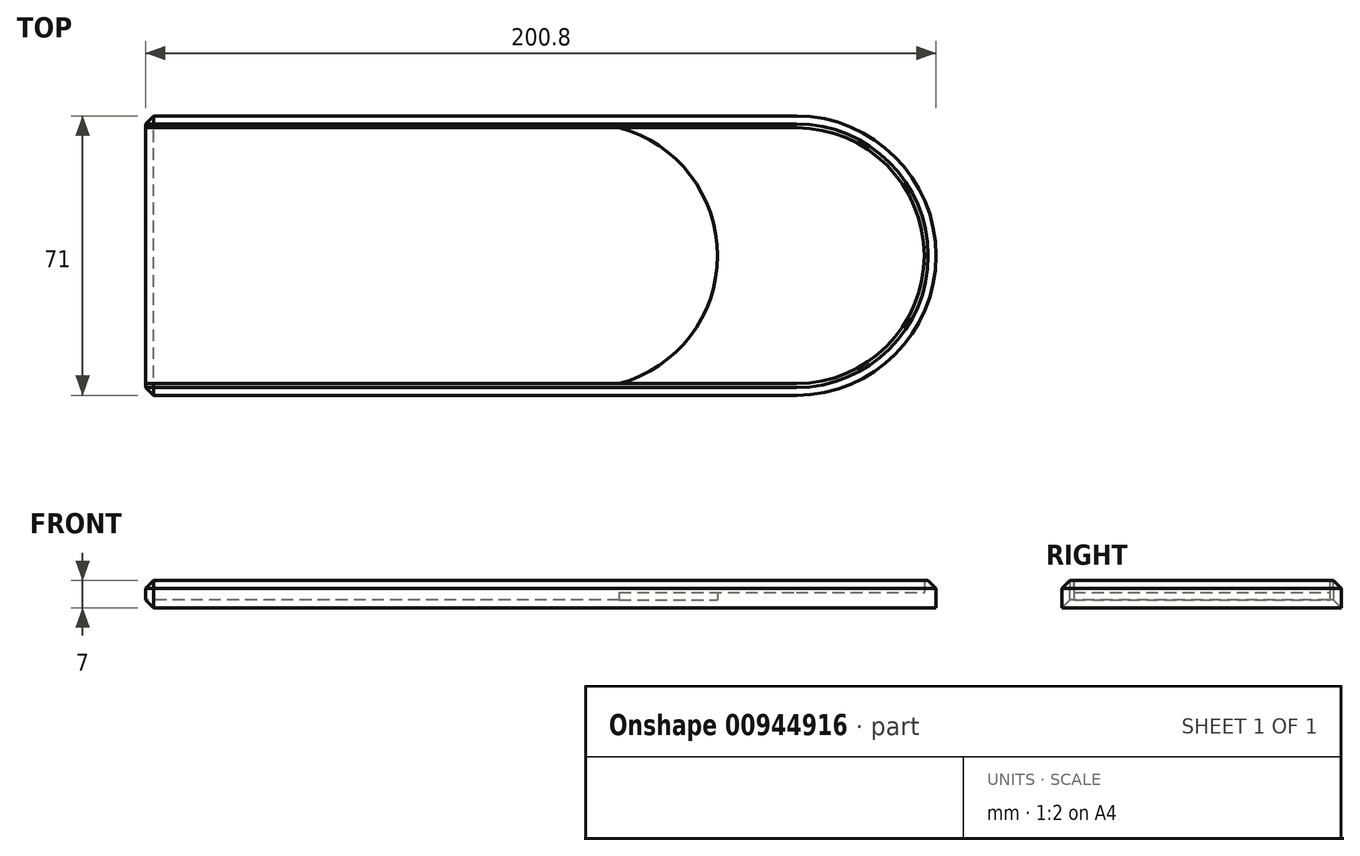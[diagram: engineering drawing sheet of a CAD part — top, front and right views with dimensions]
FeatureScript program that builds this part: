
annotation { "Feature Type Name" : "Feature", "Feature Type Description" : "" }
export const myFeature = defineFeature(function(context is Context, id is Id, definition is map)
    precondition{}
    {
        {
            var Q0;
            Q0=qCreatedBy(makeId("Top.planeOp"),FACE);
            var sketch = newSketch(context, id + "F0", { "sketchPlane" : qUnion([Q0])});
            skLineSegment(sketch, "E0.bottom", {"start": v(72.65, 32.5) * mm, "end": v(-72.65, 32.5) * mm});
            skLineSegment(sketch, "E0.top", {"start": v(72.65, -32.5) * mm, "end": v(-72.65, -32.5) * mm});
            skLineSegment(sketch, "E0.left", {"start": v(72.65, 32.5) * mm, "end": v(72.65, -32.5) * mm});
            skLineSegment(sketch, "E0.right", {"start": v(-72.65, 32.5) * mm, "end": v(-72.65, -32.5) * mm});
            skPoint(sketch, "E0.middle", {"position": v(0, 0) * mm});
            skLineSegment(sketch, "E1", {"start": v(-72.65, 32.5) * mm, "end": v(-72.65, 35.5) * mm});
            skLineSegment(sketch, "E2", {"start": v(-72.65, 35.5) * mm, "end": v(72.65, 35.5) * mm});
            skLineSegment(sketch, "E3.MirrorCS", {"start": v(-72.65, -35.5) * mm, "end": v(72.65, -35.5) * mm});
            skLineSegment(sketch, "E4.MirrorCS", {"start": v(-72.65, -32.5) * mm, "end": v(-72.65, -35.5) * mm});
            skLineSegment(sketch, "E5", {"start": v(72.65, 32.5) * mm, "end": v(92.65, 32.5) * mm});
            skLineSegment(sketch, "E6", {"start": v(72.65, 35.5) * mm, "end": v(92.65, 35.5) * mm});
            skLineSegment(sketch, "E7", {"start": v(92.65, 32.5) * mm, "end": v(92.65, 35.5) * mm});
            skPoint(sketch, "E8.MirrorCS.end.orphan", {"position": v(72.65, -35.5) * mm});
            skPoint(sketch, "E8.MirrorCS.start.orphan", {"position": v(72.65, -32.5) * mm});
            skLineSegment(sketch, "E9.MirrorCS", {"start": v(72.65, -32.5) * mm, "end": v(92.65, -32.5) * mm});
            skLineSegment(sketch, "E10.MirrorCS", {"start": v(72.65, -35.5) * mm, "end": v(92.65, -35.5) * mm});
            skLineSegment(sketch, "E11.MirrorCS", {"start": v(92.65, -32.5) * mm, "end": v(92.65, -35.5) * mm});
            skLineSegment(sketch, "E12", {"start": v(92.65, 32.5) * mm, "end": v(92.65, -32.5) * mm});
            skArc(sketch, "E13", {"start": v(92.65, -35.5) * mm, "mid": v(128.15, 0) * mm, "end": v(92.65, 35.5) * mm});
            skArc(sketch, "E14", {"start": v(92.65, -32.5) * mm, "mid": v(125.15, 0) * mm, "end": v(92.65, 32.5) * mm});
            skLineSegment(sketch, "E15", {"start": v(72.65, 35.5) * mm, "end": v(72.65, 32.5) * mm});
            skLineSegment(sketch, "E16", {"start": v(72.65, -35.5) * mm, "end": v(72.65, -32.5) * mm});
            skSolve(sketch);
        }
        {
            var Q0;
            Q0=makeQuery(id+"F0.imprint","IMPRINT",FACE,{"disambiguationData":[TD([[makeQuery(id+"F0.imprint","IMPRINT",EDGE,{"derivedFrom":sQuery(id+"F0.wireOp",EDGE,"E0.bottom")}),1.0]])]});
            extrude(context, id + "F1", {"entities" : qUnion([Q0]), "depth" : 2 * mm, "offsetDistance" : 25 * mm});
        }
        {
            var Q0;
            Q0=makeQuery(id+"F1.opExtrude","CAP_FACE",FACE,{"disambiguationData":[OSD([sQuery(id+"F0.wireOp",EDGE,"E0.bottom"),sQuery(id+"F0.wireOp",EDGE,"E0.top"),sQuery(id+"F0.wireOp",EDGE,"E0.left"),sQuery(id+"F0.wireOp",EDGE,"E0.right")])],"isStart":false});
            var sketch = newSketch(context, id + "F2", { "sketchPlane" : qUnion([Q0])});
            skLineSegment(sketch, "E17", {"start": v(72.65, 0) * mm, "end": v(47.65, 0) * mm});
            skLineSegment(sketch, "E18", {"start": v(47.65, 0) * mm, "end": v(47.65, -32.5) * mm, "construction": true});
            skLineSegment(sketch, "E19", {"start": v(47.65, -32.5) * mm, "end": v(47.65, 32.5) * mm, "construction": true});
            skArc(sketch, "E20", {"start": v(47.65, -32.5) * mm, "mid": v(72.65, 0) * mm, "end": v(47.65, 32.5) * mm});
            skSolve(sketch);
        }
        {
            var Q0;
            Q0=makeQuery(id+"F0.imprint","IMPRINT",FACE,{"disambiguationData":[TD([[makeQuery(id+"F0.imprint","IMPRINT",EDGE,{"derivedFrom":sQuery(id+"F0.wireOp",EDGE,"E0.left")}),1.0]])]});
            var Q1;
            Q1=makeQuery(id+"F0.imprint","IMPRINT",FACE,{"disambiguationData":[TD([[makeQuery(id+"F0.imprint","IMPRINT",EDGE,{"derivedFrom":sQuery(id+"F0.wireOp",EDGE,"E12")}),1.0]])]});
            extrude(context, id + "F3", {"entities" : qUnion([Q0, Q1]), "operationType" : NewBodyOperationType.ADD, "depth" : 4 * mm, "offsetDistance" : 25 * mm});
        }
        {
            var Q0;
            {var subQ0=sQuery(id+"F2.wireOp",EDGE,"E20");var subQ1=makeQuery(id+"F1.opExtrude","CAP_EDGE",EDGE,{"disambiguationData":[OSD([sQuery(id+"F0.wireOp",EDGE,"E0.left")])],"isStart":false});var subQ2=makeQuery(id+"F2.imprint","INTERSECT",VERTEX,{"derivedFrom":[subQ1,subQ0]});Q0=makeQuery(id+"F2.imprint","IMPRINT",FACE,{"disambiguationData":[TD([[makeQuery(id+"F2.imprint","IMPRINT",EDGE,{"disambiguationData":[TD([[subQ2,-1.0]])],"derivedFrom":subQ0}),-1.0]])]});}
            var Q1;
            {var subQ0=sQuery(id+"F2.wireOp",EDGE,"E20");var subQ1=makeQuery(id+"F1.opExtrude","CAP_EDGE",EDGE,{"disambiguationData":[OSD([sQuery(id+"F0.wireOp",EDGE,"E0.left")])],"isStart":false});var subQ2=makeQuery(id+"F2.imprint","INTERSECT",VERTEX,{"derivedFrom":[subQ1,subQ0]});Q1=makeQuery(id+"F2.imprint","IMPRINT",FACE,{"disambiguationData":[TD([[makeQuery(id+"F2.imprint","IMPRINT",EDGE,{"disambiguationData":[TD([[subQ2,1.0]])],"derivedFrom":subQ0}),-1.0]])]});}
            extrude(context, id + "F4", {"entities" : qUnion([Q0, Q1]), "operationType" : NewBodyOperationType.ADD, "depth" : 2 * mm, "offsetDistance" : 25 * mm});
        }
        {
            var Q0;
            Q0=makeQuery(id+"F0.imprint","IMPRINT",FACE,{"disambiguationData":[TD([[makeQuery(id+"F0.imprint","IMPRINT",EDGE,{"derivedFrom":sQuery(id+"F0.wireOp",EDGE,"E7")}),-1.0]])]});
            var Q1;
            Q1=makeQuery(id+"F0.imprint","IMPRINT",FACE,{"disambiguationData":[TD([[makeQuery(id+"F0.imprint","IMPRINT",EDGE,{"derivedFrom":sQuery(id+"F0.wireOp",EDGE,"E9.MirrorCS")}),-1.0]])]});
            var Q2;
            Q2=makeQuery(id+"F0.imprint","IMPRINT",FACE,{"disambiguationData":[TD([[makeQuery(id+"F0.imprint","IMPRINT",EDGE,{"derivedFrom":sQuery(id+"F0.wireOp",EDGE,"E5")}),1.0]])]});
            extrude(context, id + "F5", {"entities" : qUnion([Q0, Q1, Q2]), "operationType" : NewBodyOperationType.ADD, "depth" : 7 * mm, "offsetDistance" : 25 * mm});
        }
        {
            var Q0;
            Q0=makeQuery(id+"F0.imprint","IMPRINT",FACE,{"disambiguationData":[TD([[makeQuery(id+"F0.imprint","IMPRINT",EDGE,{"derivedFrom":sQuery(id+"F0.wireOp",EDGE,"E0.top")}),1.0]])]});
            var Q1;
            Q1=makeQuery(id+"F0.imprint","IMPRINT",FACE,{"disambiguationData":[TD([[makeQuery(id+"F0.imprint","IMPRINT",EDGE,{"derivedFrom":sQuery(id+"F0.wireOp",EDGE,"E0.bottom")}),-1.0]])]});
            extrude(context, id + "F6", {"entities" : qUnion([Q0, Q1]), "operationType" : NewBodyOperationType.ADD, "depth" : 7 * mm, "offsetDistance" : 25 * mm});
        }
        {
            var Q0;
            Q0=makeQuery(id+"F6.opExtrude","SWEPT_EDGE",EDGE,{"disambiguationData":[OSD([sQuery(id+"F0.wireOp",EDGE,"E1"),sQuery(id+"F0.wireOp",EDGE,"E2")])]});
            var Q1;
            Q1=makeQuery(id+"F6.opExtrude","SWEPT_EDGE",EDGE,{"disambiguationData":[OSD([sQuery(id+"F0.wireOp",EDGE,"E3.MirrorCS"),sQuery(id+"F0.wireOp",EDGE,"E4.MirrorCS")])]});
            var Q2;
            Q2=makeQuery(id+"F6.opExtrude","CAP_EDGE",EDGE,{"disambiguationData":[OSD([sQuery(id+"F0.wireOp",EDGE,"E4.MirrorCS")])],"isStart":false});
            var Q3;
            Q3=makeQuery(id+"F6.opExtrude","CAP_EDGE",EDGE,{"disambiguationData":[OSD([sQuery(id+"F0.wireOp",EDGE,"E1")])],"isStart":false});
            var Q4;
            Q4=makeQuery(id+"F6.boolean.opBoolean","MERGE",EDGE,{"derivedFrom":[makeQuery(id+"F1.opExtrude","CAP_EDGE",EDGE,{"disambiguationData":[OSD([sQuery(id+"F0.wireOp",EDGE,"E0.right")])],"isStart":true}),makeQuery(id+"F6.opExtrude","CAP_EDGE",EDGE,{"disambiguationData":[OSD([sQuery(id+"F0.wireOp",EDGE,"E1")])],"isStart":true}),makeQuery(id+"F6.opExtrude","CAP_EDGE",EDGE,{"disambiguationData":[OSD([sQuery(id+"F0.wireOp",EDGE,"E4.MirrorCS")])],"isStart":true})]});
            var Q5;
            Q5=makeQuery(id+"F6.boolean.opBoolean","MERGE",EDGE,{"derivedFrom":[makeQuery(id+"F5.opExtrude","CAP_EDGE",EDGE,{"disambiguationData":[OSD([sQuery(id+"F0.wireOp",EDGE,"E6")])],"isStart":false}),makeQuery(id+"F6.opExtrude","CAP_EDGE",EDGE,{"disambiguationData":[OSD([sQuery(id+"F0.wireOp",EDGE,"E2")])],"isStart":false})]});
            chamfer(context, id + "F7", {"entities" : qUnion([Q0, Q1, Q2, Q3, Q4, Q5]), "width" : 2 * mm, "tangentPropagation" : true});
        }
    });
